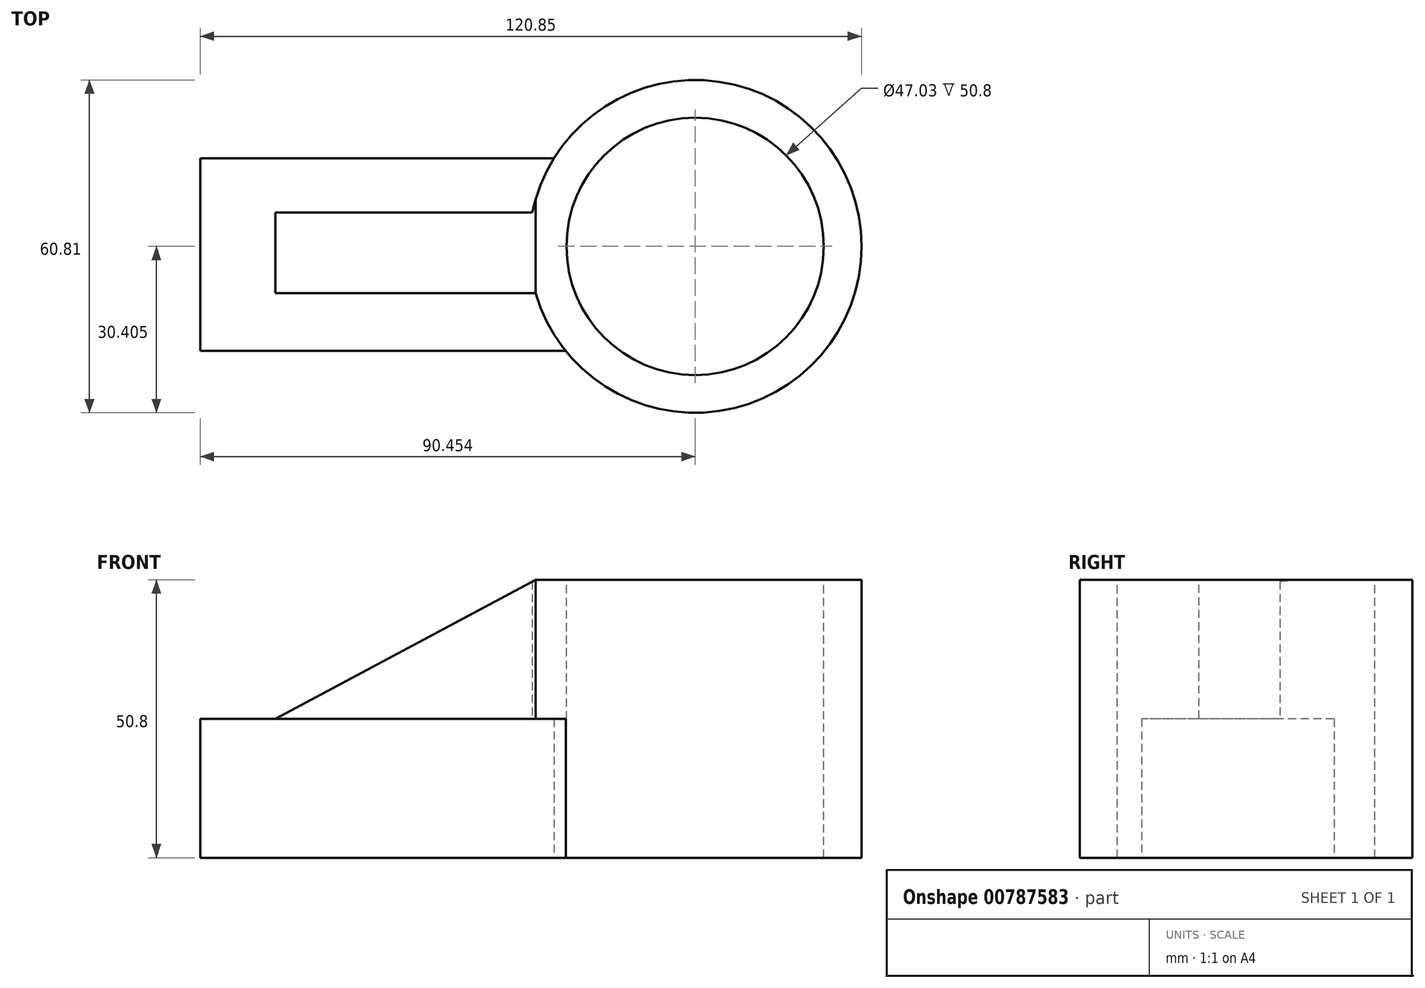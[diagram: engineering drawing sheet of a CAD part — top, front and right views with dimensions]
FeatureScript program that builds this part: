
annotation { "Feature Type Name" : "Feature", "Feature Type Description" : "" }
export const myFeature = defineFeature(function(context is Context, id is Id, definition is map)
    precondition{}
    {
        {
            var Q0;
            Q0=qCreatedBy(makeId("Top.planeOp"),FACE);
            var sketch = newSketch(context, id + "F0", { "sketchPlane" : qUnion([Q0])});
            skLineSegment(sketch, "E0", {"start": v(-45.9, 13.13) * mm, "end": v(-45.9, -22.05) * mm});
            skLineSegment(sketch, "E1", {"start": v(-45.9, -22.05) * mm, "end": v(36.51, -22.05) * mm});
            skLineSegment(sketch, "E2", {"start": v(-45.9, 13.13) * mm, "end": v(36.51, 13.13) * mm});
            skCircle(sketch, "E3", {"center": v(36.51, -3.5) * mm, "radius": 20.6 * mm});
            skCircle(sketch, "E4", {"center": v(36.51, -3.5) * mm, "radius": 16.63 * mm});
            skSolve(sketch);
        }
        {
            var Q0;
            {var subQ0=sQuery(id+"F0.wireOp",EDGE,"E0");Q0=makeQuery(id+"F0.imprint","IMPRINT",FACE,{"disambiguationData":[TD([[makeQuery(id+"F0.imprint","IMPRINT",EDGE,{"derivedFrom":subQ0}),1.0]])]});}
            extrude(context, id + "F1", {"entities" : qUnion([Q0]), "depth" : 25.4 * mm, "offsetDistance" : 25.4 * mm});
        }
        {
            var Q0;
            Q0=qCreatedBy(makeId("Top.planeOp"),FACE);
            var sketch = newSketch(context, id + "F2", { "sketchPlane" : qUnion([Q0])});
            skCircle(sketch, "E5", {"center": v(44.54, -2.95) * mm, "radius": 30.4 * mm});
            skSolve(sketch);
        }
        {
            var Q0;
            Q0=makeQuery(id+"F2.imprint","IMPRINT",FACE,{"disambiguationData":[TD([[makeQuery(id+"F2.imprint","IMPRINT",EDGE,{"derivedFrom":sQuery(id+"F2.wireOp",EDGE,"E5")}),1.0]])]});
            extrude(context, id + "F3", {"entities" : qUnion([Q0]), "operationType" : NewBodyOperationType.ADD, "depth" : 50.8 * mm, "offsetDistance" : 25.4 * mm});
        }
        {
            var Q0;
            Q0=makeQuery(id+"F3.opExtrude","CAP_FACE",FACE,{"disambiguationData":[OSD([sQuery(id+"F2.wireOp",EDGE,"E5")])],"isStart":false});
            var sketch = newSketch(context, id + "F4", { "sketchPlane" : qUnion([Q0])});
            skCircle(sketch, "E6", {"center": v(44.54, -2.95) * mm, "radius": 23.51 * mm});
            skSolve(sketch);
        }
        {
            var Q0;
            Q0=makeQuery(id+"F4.imprint","IMPRINT",FACE,{"disambiguationData":[TD([[makeQuery(id+"F4.imprint","IMPRINT",EDGE,{"derivedFrom":sQuery(id+"F4.wireOp",EDGE,"E6")}),1.0]])]});
            extrude(context, id + "F5", {"entities" : qUnion([Q0]), "operationType" : NewBodyOperationType.REMOVE, "oppositeDirection" : true, "depth" : 1676.4 * mm, "offsetDistance" : 25.4 * mm});
        }
        {
            var Q0;
            Q0=makeQuery(id+"F1.opExtrude","CAP_FACE",FACE,{"disambiguationData":[OSD([sQuery(id+"F0.wireOp",EDGE,"E0"),sQuery(id+"F0.wireOp",EDGE,"E1"),sQuery(id+"F0.wireOp",EDGE,"E2"),sQuery(id+"F0.wireOp",EDGE,"E3")])],"isStart":false});
            var sketch = newSketch(context, id + "F6", { "sketchPlane" : qUnion([Q0])});
            skLineSegment(sketch, "E7.bottom", {"start": v(-32.17, 3.25) * mm, "end": v(15.38, 3.25) * mm});
            skLineSegment(sketch, "E7.top", {"start": v(-32.17, -11.52) * mm, "end": v(15.38, -11.52) * mm});
            skLineSegment(sketch, "E7.left", {"start": v(-32.17, 3.25) * mm, "end": v(-32.17, -11.52) * mm});
            skLineSegment(sketch, "E7.right", {"start": v(15.38, 3.25) * mm, "end": v(15.38, -11.52) * mm});
            skSolve(sketch);
        }
        {
            var Q0;
            {var subQ4=sQuery(id+"F6.wireOp",EDGE,"E7.top");Q0=makeQuery(id+"F6.imprint","IMPRINT",FACE,{"disambiguationData":[TD([[makeQuery(id+"F6.imprint","IMPRINT",EDGE,{"derivedFrom":subQ4}),1.0]])]});}
            extrude(context, id + "F7", {"entities" : qUnion([Q0]), "operationType" : NewBodyOperationType.ADD, "depth" : 25.4 * mm, "offsetDistance" : 25.4 * mm});
        }
        {
            var Q0;
            Q0=makeQuery(id+"F7.opExtrude","SWEPT_FACE",FACE,{"disambiguationData":[OSD([sQuery(id+"F6.wireOp",EDGE,"E7.top")])]});
            var sketch = newSketch(context, id + "F8", { "sketchPlane" : qUnion([Q0])});
            skLineSegment(sketch, "E8", {"start": v(-32.17, 25.4) * mm, "end": v(15.38, 50.8) * mm});
            skSolve(sketch);
        }
        {
            var Q0;
            Q0=makeQuery(id+"F8.imprint","IMPRINT",FACE,{"disambiguationData":[TD([[makeQuery(id+"F8.imprint","IMPRINT",EDGE,{"derivedFrom":sQuery(id+"F8.wireOp",EDGE,"E8")}),1.0]])]});
            extrude(context, id + "F9", {"entities" : qUnion([Q0]), "operationType" : NewBodyOperationType.REMOVE, "oppositeDirection" : true, "depth" : 2514.6 * mm, "offsetDistance" : 25.4 * mm});
        }
    });
